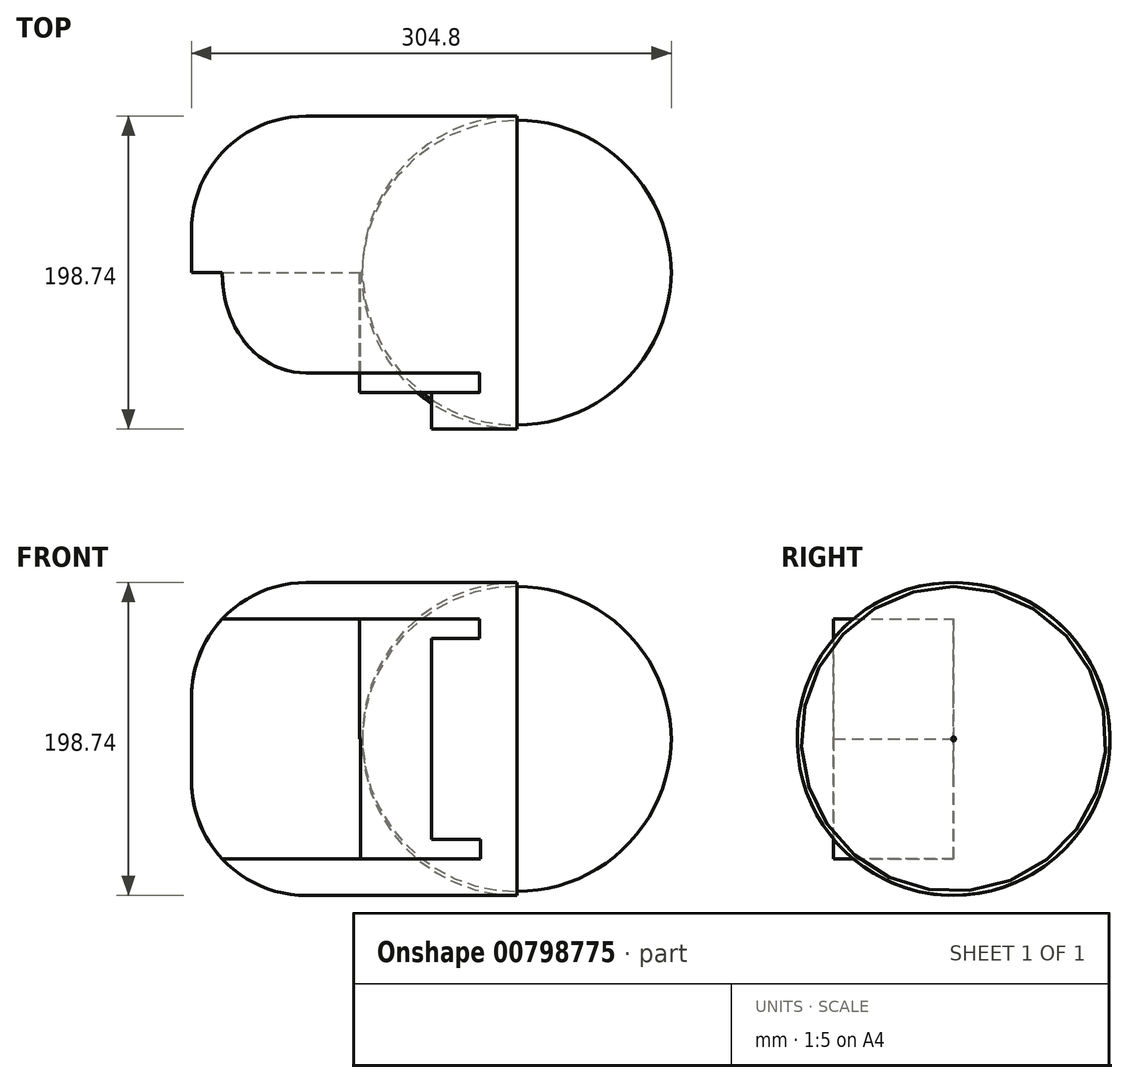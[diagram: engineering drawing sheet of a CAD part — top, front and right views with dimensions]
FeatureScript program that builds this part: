
annotation { "Feature Type Name" : "Feature", "Feature Type Description" : "" }
export const myFeature = defineFeature(function(context is Context, id is Id, definition is map)
    precondition{}
    {
        {
            var Q0;
            Q0=qCreatedBy(makeId("Front.planeOp"),FACE);
            var sketch = newSketch(context, id + "F0", { "sketchPlane" : qUnion([Q0])});
            skLineSegment(sketch, "E0.bottom", {"start": v(-45.57, 76.2) * mm, "end": v(30.63, 76.2) * mm});
            skLineSegment(sketch, "E0.top", {"start": v(-45.57, 0) * mm, "end": v(30.63, 0) * mm});
            skLineSegment(sketch, "E0.left", {"start": v(-45.57, 76.2) * mm, "end": v(-45.57, 0) * mm});
            skLineSegment(sketch, "E0.right", {"start": v(30.63, 76.2) * mm, "end": v(30.63, 0) * mm});
            skSolve(sketch);
        }
        {
            var Q0;
            Q0=makeQuery(id+"F0.imprint","IMPRINT",FACE,{"disambiguationData":[TD([[makeQuery(id+"F0.imprint","IMPRINT",EDGE,{"derivedFrom":sQuery(id+"F0.wireOp",EDGE,"E0.bottom")}),-1.0]])]});
            extrude(context, id + "F1", {"entities" : qUnion([Q0]), "depth" : 76.2 * mm, "offsetDistance" : 25.4 * mm});
        }
        {
            var Q0;
            Q0=qCreatedBy(makeId("Front.planeOp"),FACE);
            var sketch = newSketch(context, id + "F2", { "sketchPlane" : qUnion([Q0])});
            skLineSegment(sketch, "E1.bottom", {"start": v(-44.82, 0) * mm, "end": v(31.38, 0) * mm});
            skLineSegment(sketch, "E1.top", {"start": v(-44.82, -76.2) * mm, "end": v(31.38, -76.2) * mm});
            skLineSegment(sketch, "E1.left", {"start": v(-44.82, 0) * mm, "end": v(-44.82, -76.2) * mm});
            skLineSegment(sketch, "E1.right", {"start": v(31.38, 0) * mm, "end": v(31.38, -76.2) * mm});
            skSolve(sketch);
        }
        {
            var Q0;
            Q0=makeQuery(id+"F2.imprint","IMPRINT",FACE,{"disambiguationData":[TD([[makeQuery(id+"F2.imprint","IMPRINT",EDGE,{"derivedFrom":sQuery(id+"F2.wireOp",EDGE,"E1.bottom")}),-1.0]])]});
            extrude(context, id + "F3", {"entities" : qUnion([Q0]), "operationType" : NewBodyOperationType.ADD, "depth" : 76.2 * mm, "offsetDistance" : 25.4 * mm});
        }
        {
            var Q0;
            Q0=qCreatedBy(makeId("Right.planeOp"),FACE);
            var sketch = newSketch(context, id + "F4", { "sketchPlane" : qUnion([Q0])});
            skCircle(sketch, "E2", {"center": v(0, 0) * mm, "radius": 99.37 * mm});
            skSolve(sketch);
        }
        {
            var Q0;
            Q0=makeQuery(id+"F4.imprint","IMPRINT",FACE,{"disambiguationData":[TD([[makeQuery(id+"F4.imprint","IMPRINT",EDGE,{"derivedFrom":sQuery(id+"F4.wireOp",EDGE,"E2")}),1.0]])]});
            extrude(context, id + "F5", {"entities" : qUnion([Q0]), "operationType" : NewBodyOperationType.ADD, "depth" : 152.4 * mm, "offsetDistance" : 25.4 * mm});
        }
        {
            var Q0;
            {var subQ1=sQuery(id+"F0.wireOp",EDGE,"E0.bottom");var subQ2=sQuery(id+"F4.wireOp",EDGE,"E2");Q0=makeQuery(id+"F5.boolean.opBoolean","SPLIT",FACE,{"disambiguationData":[TD([makeQuery(id+"F1.opExtrude","SWEPT_FACE",FACE,{"disambiguationData":[OSD([subQ1])]})])],"derivedFrom":makeQuery(id+"F5.opExtrude","CAP_FACE",FACE,{"disambiguationData":[OSD([subQ2])],"isStart":true})});}
            extrude(context, id + "F6", {"entities" : qUnion([Q0]), "operationType" : NewBodyOperationType.ADD, "depth" : 152.4 * mm, "offsetDistance" : 25.4 * mm});
        }
        {
            var Q0;
            Q0=makeQuery(id+"F6.opExtrude","CAP_EDGE",EDGE,{"disambiguationData":[OSD([sQuery(id+"F4.wireOp",EDGE,"E2")])],"isStart":false});
            fillet(context, id + "F7", {"entities" : qUnion([Q0]), "radius" : 72.97 * mm, "tangentPropagation" : true, "allowEdgeOverflow" : false});
        }
        {
            var Q0;
            Q0=makeQuery(id+"F5.opExtrude","CAP_EDGE",EDGE,{"disambiguationData":[OSD([sQuery(id+"F4.wireOp",EDGE,"E2")])],"isStart":false});
            fillet(context, id + "F8", {"entities" : qUnion([Q0]), "radius" : 98.11 * mm, "tangentPropagation" : true, "allowEdgeOverflow" : false});
        }
    });
